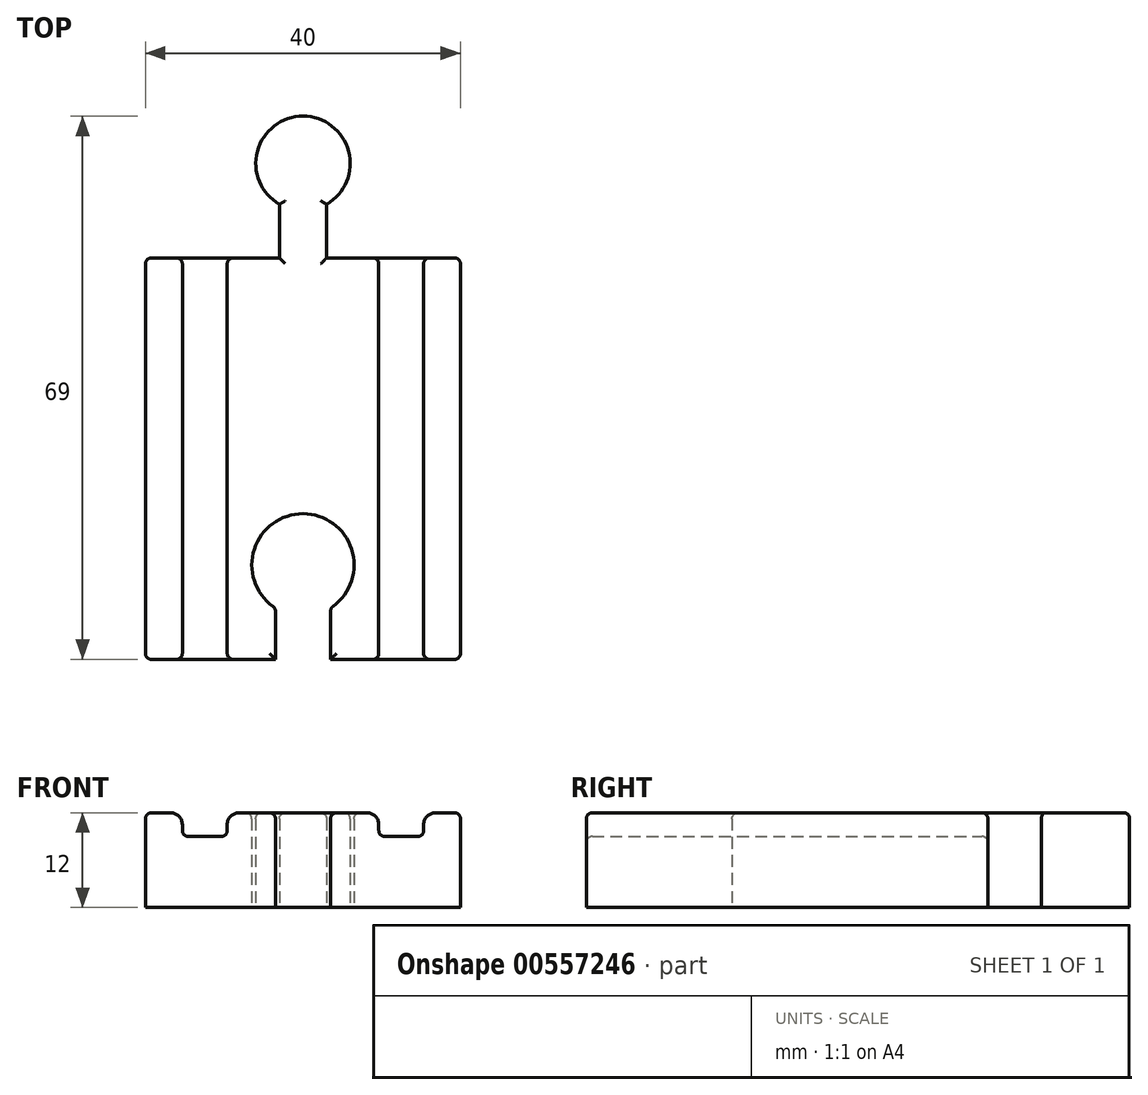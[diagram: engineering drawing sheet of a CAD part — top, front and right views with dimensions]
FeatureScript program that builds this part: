
annotation { "Feature Type Name" : "Feature", "Feature Type Description" : "" }
export const myFeature = defineFeature(function(context is Context, id is Id, definition is map)
    precondition{}
    {
        {
            assignVariable(context, id + "F0", {"name" : "wood_height", "anyValue" : 12});
        }
        {
            var Q0;
            Q0=qCreatedBy(makeId("Front.planeOp"),FACE);
            var sketch = newSketch(context, id + "F1", { "sketchPlane" : qUnion([Q0])});
            skLineSegment(sketch, "E0.bottom", {"start": v(-20, 12) * mm, "end": v(-16.82, 12) * mm});
            skLineSegment(sketch, "E0.top", {"start": v(-20, 0) * mm, "end": v(20, 0) * mm});
            skLineSegment(sketch, "E0.left", {"start": v(-20, 12) * mm, "end": v(-20, 0) * mm});
            skLineSegment(sketch, "E0.right", {"start": v(20, 12) * mm, "end": v(20, 0) * mm});
            skLineSegment(sketch, "E1.top", {"start": v(-15.32, 9) * mm, "end": v(-9.62, 9) * mm});
            skLineSegment(sketch, "E1.left", {"start": v(-15.32, 10.5) * mm, "end": v(-15.32, 9) * mm});
            skLineSegment(sketch, "E1.right", {"start": v(-9.62, 10.5) * mm, "end": v(-9.62, 9) * mm});
            skLineSegment(sketch, "E2.trimOffspring", {"start": v(-8.12, 12) * mm, "end": v(8.12, 12) * mm});
            skPoint(sketch, "E3", {"position": v(0, 12) * mm});
            skLineSegment(sketch, "E4.MirrorCS", {"start": v(9.62, 10.5) * mm, "end": v(9.62, 9) * mm});
            skLineSegment(sketch, "E5.MirrorCS", {"start": v(15.32, 10.5) * mm, "end": v(15.32, 9) * mm});
            skLineSegment(sketch, "E6.MirrorCS", {"start": v(15.32, 9) * mm, "end": v(9.62, 9) * mm});
            skLineSegment(sketch, "E7.trimOffspring", {"start": v(16.82, 12) * mm, "end": v(20, 12) * mm});
            skArc(sketch, "E8.filletArc", {"start": v(-15.32, 10.5) * mm, "mid": v(-15.76, 11.56) * mm, "end": v(-16.82, 12) * mm});
            skArc(sketch, "E9.filletArc", {"start": v(-8.12, 12) * mm, "mid": v(-9.19, 11.56) * mm, "end": v(-9.62, 10.5) * mm});
            skArc(sketch, "E10.filletArc", {"start": v(9.62, 10.5) * mm, "mid": v(9.19, 11.56) * mm, "end": v(8.12, 12) * mm});
            skArc(sketch, "E11.filletArc", {"start": v(16.82, 12) * mm, "mid": v(15.76, 11.56) * mm, "end": v(15.32, 10.5) * mm});
            skSolve(sketch);
        }
        {
            var Q0;
            Q0=makeQuery(id+"F1.imprint","IMPRINT",FACE,{"disambiguationData":[TD([[makeQuery(id+"F1.imprint","IMPRINT",EDGE,{"derivedFrom":sQuery(id+"F1.wireOp",EDGE,"E0.bottom")}),-1.0]])]});
            extrude(context, id + "F2", {"entities" : qUnion([Q0]), "depth" : 51 * mm, "offsetDistance" : 25 * mm});
        }
        {
            var Q0;
            Q0=qCreatedBy(makeId("Top.planeOp"),FACE);
            var sketch = newSketch(context, id + "F3", { "sketchPlane" : qUnion([Q0])});
            skLineSegment(sketch, "E12.bottom", {"start": v(3, 0) * mm, "end": v(-3, 0) * mm});
            skLineSegment(sketch, "E12.top", {"start": v(3, 6.8) * mm, "end": v(-3, 6.8) * mm});
            skLineSegment(sketch, "E12.left", {"start": v(3, 0) * mm, "end": v(3, 6.8) * mm});
            skLineSegment(sketch, "E12.right", {"start": v(-3, 0) * mm, "end": v(-3, 6.8) * mm});
            skCircle(sketch, "E13", {"center": v(0, 12) * mm, "radius": 6 * mm});
            skSolve(sketch);
        }
        {
            var Q0;
            Q0 = qSketchRegion(id + "F3", true);
            extrude(context, id + "F4", {"entities" : qUnion([Q0]), "depth" : getVariable(context, 'wood_height') * mm, "offsetDistance" : 25 * mm});
        }
        {
            var Q0;
            Q0=makeQuery(id+"F4.opExtrude","SWEPT_BODY",BODY,{"disambiguationData":[OSD([sQuery(id+"F3.wireOp",EDGE,"E12.bottom"),sQuery(id+"F3.wireOp",EDGE,"E12.left"),sQuery(id+"F3.wireOp",EDGE,"E12.right"),sQuery(id+"F3.wireOp",EDGE,"E13")])]});
            var Q1;
            Q1=makeQuery(id+"F2.opExtrude","SWEPT_BODY",BODY,{"disambiguationData":[OSD([sQuery(id+"F1.wireOp",EDGE,"E0.bottom"),sQuery(id+"F1.wireOp",EDGE,"E0.top"),sQuery(id+"F1.wireOp",EDGE,"E0.left"),sQuery(id+"F1.wireOp",EDGE,"E0.right"),sQuery(id+"F1.wireOp",EDGE,"E1.top"),sQuery(id+"F1.wireOp",EDGE,"E1.left"),sQuery(id+"F1.wireOp",EDGE,"E1.right"),sQuery(id+"F1.wireOp",EDGE,"E2.trimOffspring"),sQuery(id+"F1.wireOp",EDGE,"E4.MirrorCS"),sQuery(id+"F1.wireOp",EDGE,"E5.MirrorCS"),sQuery(id+"F1.wireOp",EDGE,"E6.MirrorCS"),sQuery(id+"F1.wireOp",EDGE,"E7.trimOffspring"),sQuery(id+"F1.wireOp",EDGE,"E8.filletArc"),sQuery(id+"F1.wireOp",EDGE,"E9.filletArc"),sQuery(id+"F1.wireOp",EDGE,"E10.filletArc"),sQuery(id+"F1.wireOp",EDGE,"E11.filletArc")])]});
            booleanBodies(context, id + "F5", {"operationType" : BooleanOperationType.UNION, "tools" : qUnion([Q0, Q1])});
        }
        {
            var Q0;
            Q0=makeQuery(id+"F5.opBoolean","MERGE",FACE,{"derivedFrom":[makeQuery(id+"F2.opExtrude","SWEPT_FACE",FACE,{"disambiguationData":[OSD([sQuery(id+"F1.wireOp",EDGE,"E0.top")])]}),makeQuery(id+"F4.opExtrude","CAP_FACE",FACE,{"disambiguationData":[OSD([sQuery(id+"F3.wireOp",EDGE,"E12.bottom"),sQuery(id+"F3.wireOp",EDGE,"E12.left"),sQuery(id+"F3.wireOp",EDGE,"E12.right"),sQuery(id+"F3.wireOp",EDGE,"E13")])],"isStart":true})]});
            var sketch = newSketch(context, id + "F6", { "sketchPlane" : qUnion([Q0])});
            skLineSegment(sketch, "E14.bottom", {"start": v(-3.5, 51) * mm, "end": v(3.5, 51) * mm});
            skLineSegment(sketch, "E14.top", {"start": v(-3.5, 44.48) * mm, "end": v(3.5, 44.48) * mm});
            skLineSegment(sketch, "E14.left", {"start": v(-3.5, 51) * mm, "end": v(-3.5, 44.48) * mm});
            skLineSegment(sketch, "E14.right", {"start": v(3.5, 51) * mm, "end": v(3.5, 44.48) * mm});
            skCircle(sketch, "E15", {"center": v(0, 39) * mm, "radius": 6.5 * mm});
            skSolve(sketch);
        }
        {
            var Q0;
            Q0 = qSketchRegion(id + "F6", true);
            extrude(context, id + "F7", {"entities" : qUnion([Q0]), "operationType" : NewBodyOperationType.REMOVE, "oppositeDirection" : true, "depth" : (getVariable(context, 'wood_height')) * mm, "offsetDistance" : 25 * mm});
        }
        {
            var Q0;
            Q0=makeQuery(id+"F5.opBoolean","MERGE",FACE,{"derivedFrom":[makeQuery(id+"F2.opExtrude","SWEPT_FACE",FACE,{"disambiguationData":[OSD([sQuery(id+"F1.wireOp",EDGE,"E2.trimOffspring")])]}),makeQuery(id+"F4.opExtrude","CAP_FACE",FACE,{"disambiguationData":[OSD([sQuery(id+"F3.wireOp",EDGE,"E12.bottom"),sQuery(id+"F3.wireOp",EDGE,"E12.left"),sQuery(id+"F3.wireOp",EDGE,"E12.right"),sQuery(id+"F3.wireOp",EDGE,"E13")])],"isStart":false})]});
            var Q1;
            Q1=makeQuery(id+"F2.opExtrude","SWEPT_FACE",FACE,{"disambiguationData":[OSD([sQuery(id+"F1.wireOp",EDGE,"E6.MirrorCS")])]});
            var Q2;
            Q2=makeQuery(id+"F2.opExtrude","SWEPT_FACE",FACE,{"disambiguationData":[OSD([sQuery(id+"F1.wireOp",EDGE,"E7.trimOffspring")])]});
            var Q3;
            Q3=makeQuery(id+"F2.opExtrude","SWEPT_FACE",FACE,{"disambiguationData":[OSD([sQuery(id+"F1.wireOp",EDGE,"E0.bottom")])]});
            var Q4;
            Q4=makeQuery(id+"F2.opExtrude","SWEPT_FACE",FACE,{"disambiguationData":[OSD([sQuery(id+"F1.wireOp",EDGE,"E1.top")])]});
            var Q5;
            Q5=makeQuery(id+"F7.boolean.opBoolean","COPY",EDGE,{"derivedFrom":makeQuery(id+"F7.opExtrude","SWEPT_EDGE",EDGE,{"disambiguationData":[OSD([sQuery(id+"F6.wireOp",EDGE,"E14.top"),sQuery(id+"F6.wireOp",EDGE,"E14.left"),sQuery(id+"F6.wireOp",EDGE,"E15")])]})});
            var Q6;
            Q6=makeQuery(id+"F7.boolean.opBoolean","COPY",EDGE,{"derivedFrom":makeQuery(id+"F7.opExtrude","SWEPT_EDGE",EDGE,{"disambiguationData":[OSD([sQuery(id+"F6.wireOp",EDGE,"E14.top"),sQuery(id+"F6.wireOp",EDGE,"E14.right"),sQuery(id+"F6.wireOp",EDGE,"E15")])]})});
            var Q7;
            Q7=makeQuery(id+"F2.opExtrude","CAP_EDGE",EDGE,{"disambiguationData":[OSD([sQuery(id+"F1.wireOp",EDGE,"E0.right")])],"isStart":false});
            var Q8;
            Q8=makeQuery(id+"F2.opExtrude","CAP_EDGE",EDGE,{"disambiguationData":[OSD([sQuery(id+"F1.wireOp",EDGE,"E0.right")])],"isStart":true});
            var Q9;
            Q9=makeQuery(id+"F2.opExtrude","CAP_EDGE",EDGE,{"disambiguationData":[OSD([sQuery(id+"F1.wireOp",EDGE,"E0.left")])],"isStart":true});
            var Q10;
            Q10=makeQuery(id+"F2.opExtrude","CAP_EDGE",EDGE,{"disambiguationData":[OSD([sQuery(id+"F1.wireOp",EDGE,"E0.left")])],"isStart":false});
            var Q11;
            Q11=makeQuery(id+"F7.boolean.opBoolean","COPY",EDGE,{"derivedFrom":makeQuery(id+"F7.opExtrude","SWEPT_EDGE",EDGE,{"disambiguationData":[OSD([sQuery(id+"F1.wireOp",EDGE,"E0.top"),sQuery(id+"F6.wireOp",EDGE,"E14.bottom"),sQuery(id+"F6.wireOp",EDGE,"E14.left")])]})});
            var Q12;
            Q12=makeQuery(id+"F7.boolean.opBoolean","COPY",EDGE,{"derivedFrom":makeQuery(id+"F7.opExtrude","SWEPT_EDGE",EDGE,{"disambiguationData":[OSD([sQuery(id+"F1.wireOp",EDGE,"E0.top"),sQuery(id+"F6.wireOp",EDGE,"E14.bottom"),sQuery(id+"F6.wireOp",EDGE,"E14.right")])]})});
            fillet(context, id + "F8", {"entities" : qUnion([Q0, Q1, Q2, Q3, Q4, Q5, Q6, Q7, Q8, Q9, Q10, Q11, Q12]), "radius" : .75 * mm, "tangentPropagation" : true, "allowEdgeOverflow" : false});
        }
    });
